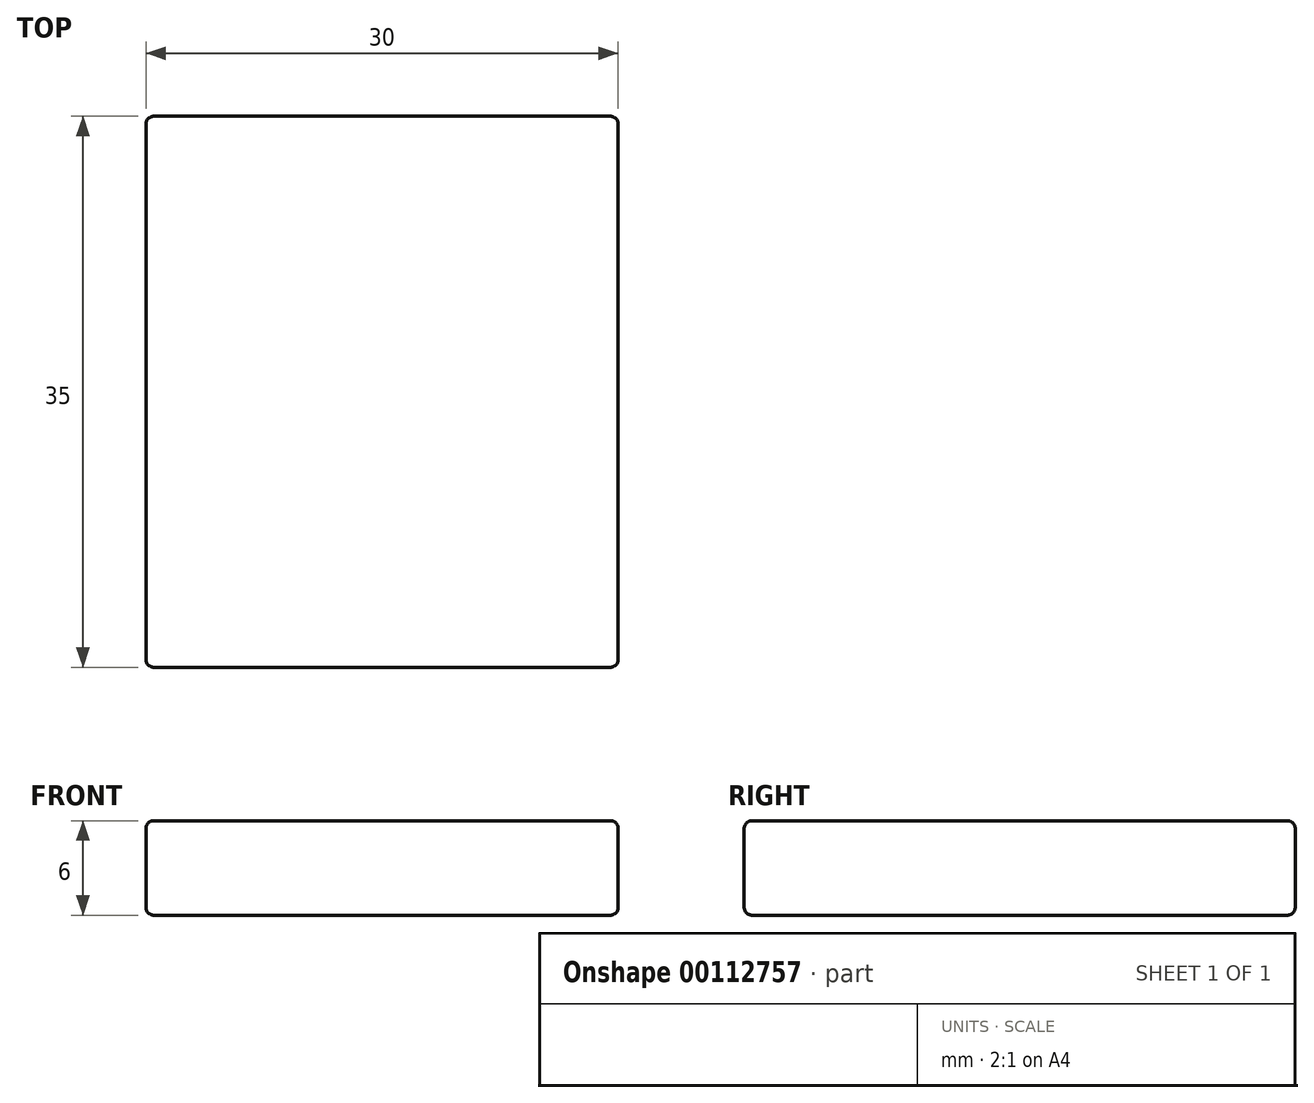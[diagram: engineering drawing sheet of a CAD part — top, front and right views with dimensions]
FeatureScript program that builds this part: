
annotation { "Feature Type Name" : "Feature", "Feature Type Description" : "" }
export const myFeature = defineFeature(function(context is Context, id is Id, definition is map)
    precondition{}
    {
        {
            var Q0;
            Q0=qCreatedBy(makeId("Top.planeOp"),FACE);
            var sketch = newSketch(context, id + "F0", { "sketchPlane" : qUnion([Q0])});
            skLineSegment(sketch, "E0.bottom", {"start": v(-15, 17.5) * mm, "end": v(15, 17.5) * mm});
            skLineSegment(sketch, "E0.top", {"start": v(-15, -17.5) * mm, "end": v(15, -17.5) * mm});
            skLineSegment(sketch, "E0.left", {"start": v(-15, 17.5) * mm, "end": v(-15, -17.5) * mm});
            skLineSegment(sketch, "E0.right", {"start": v(15, 17.5) * mm, "end": v(15, -17.5) * mm});
            skPoint(sketch, "E0.middle", {"position": v(0, 0) * mm});
            skSolve(sketch);
        }
        {
            var Q0;
            Q0 = qSketchRegion(id + "F0", true);
            extrude(context, id + "F1", {"entities" : qUnion([Q0]), "depth" : 6 * mm});
        }
        {
            var Q0;
            Q0=makeQuery(id+"F1.opExtrude","CAP_EDGE",EDGE,{"disambiguationData":[OSD([sQuery(id+"F0.wireOp",EDGE,"E0.left")])],"isStart":false});
            var Q1;
            Q1=makeQuery(id+"F1.opExtrude","CAP_EDGE",EDGE,{"disambiguationData":[OSD([sQuery(id+"F0.wireOp",EDGE,"E0.top")])],"isStart":false});
            var Q2;
            Q2=makeQuery(id+"F1.opExtrude","CAP_EDGE",EDGE,{"disambiguationData":[OSD([sQuery(id+"F0.wireOp",EDGE,"E0.top")])],"isStart":true});
            var Q3;
            Q3=makeQuery(id+"F1.opExtrude","CAP_EDGE",EDGE,{"disambiguationData":[OSD([sQuery(id+"F0.wireOp",EDGE,"E0.left")])],"isStart":true});
            var Q4;
            Q4=makeQuery(id+"F1.opExtrude","SWEPT_EDGE",EDGE,{"disambiguationData":[OSD([sQuery(id+"F0.wireOp",EDGE,"E0.top"),sQuery(id+"F0.wireOp",EDGE,"E0.left")])]});
            var Q5;
            Q5=makeQuery(id+"F1.opExtrude","CAP_EDGE",EDGE,{"disambiguationData":[OSD([sQuery(id+"F0.wireOp",EDGE,"E0.right")])],"isStart":false});
            var Q6;
            Q6=makeQuery(id+"F1.opExtrude","SWEPT_EDGE",EDGE,{"disambiguationData":[OSD([sQuery(id+"F0.wireOp",EDGE,"E0.top"),sQuery(id+"F0.wireOp",EDGE,"E0.right")])]});
            var Q7;
            Q7=makeQuery(id+"F1.opExtrude","CAP_EDGE",EDGE,{"disambiguationData":[OSD([sQuery(id+"F0.wireOp",EDGE,"E0.right")])],"isStart":true});
            var Q8;
            Q8=makeQuery(id+"F1.opExtrude","SWEPT_EDGE",EDGE,{"disambiguationData":[OSD([sQuery(id+"F0.wireOp",EDGE,"E0.bottom"),sQuery(id+"F0.wireOp",EDGE,"E0.right")])]});
            var Q9;
            Q9=makeQuery(id+"F1.opExtrude","CAP_EDGE",EDGE,{"disambiguationData":[OSD([sQuery(id+"F0.wireOp",EDGE,"E0.bottom")])],"isStart":false});
            var Q10;
            Q10=makeQuery(id+"F1.opExtrude","CAP_EDGE",EDGE,{"disambiguationData":[OSD([sQuery(id+"F0.wireOp",EDGE,"E0.bottom")])],"isStart":true});
            var Q11;
            Q11=makeQuery(id+"F1.opExtrude","SWEPT_EDGE",EDGE,{"disambiguationData":[OSD([sQuery(id+"F0.wireOp",EDGE,"E0.bottom"),sQuery(id+"F0.wireOp",EDGE,"E0.left")])]});
            fillet(context, id + "F2", {"entities" : qUnion([Q0, Q1, Q2, Q3, Q4, Q5, Q6, Q7, Q8, Q9, Q10, Q11]), "radius" : 0.5 * mm, "tangentPropagation" : true, "allowEdgeOverflow" : false});
        }
    });
